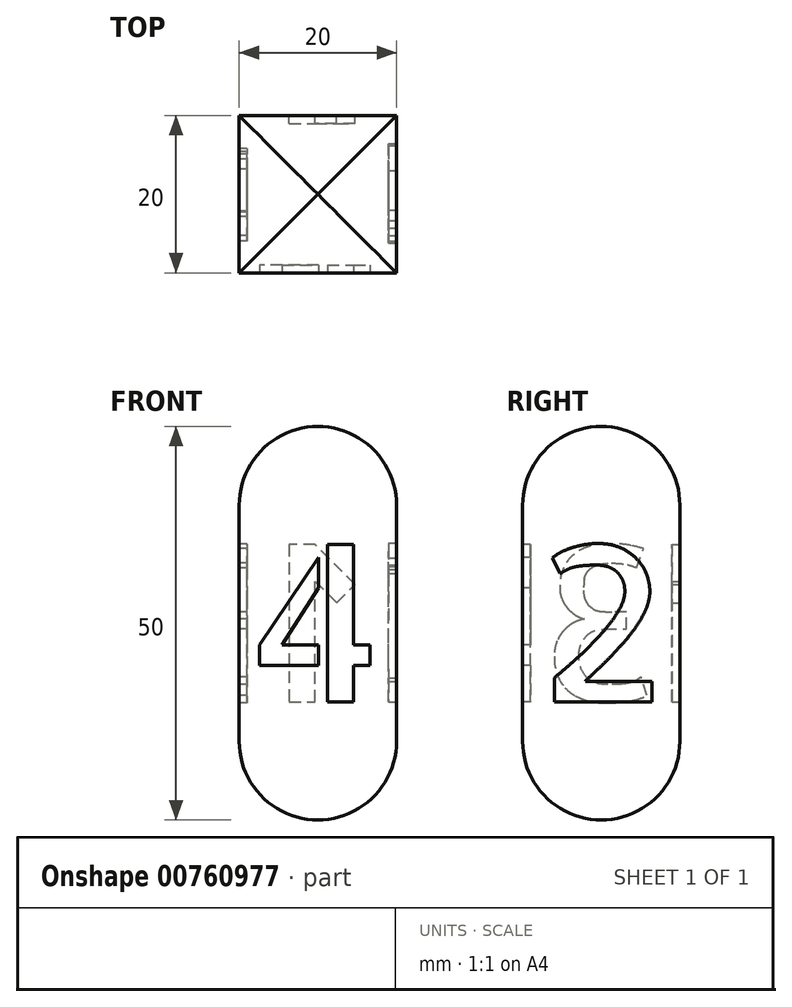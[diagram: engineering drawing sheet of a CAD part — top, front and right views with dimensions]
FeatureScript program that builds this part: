
annotation { "Feature Type Name" : "Feature", "Feature Type Description" : "" }
export const myFeature = defineFeature(function(context is Context, id is Id, definition is map)
    precondition{}
    {
        {
            var Q0;
            Q0=qCreatedBy(makeId("Top.planeOp"),FACE);
            var sketch = newSketch(context, id + "F0", { "sketchPlane" : qUnion([Q0])});
            skLineSegment(sketch, "E0.bottom", {"start": v(0, 0) * mm, "end": v(-20, 0) * mm});
            skLineSegment(sketch, "E0.top", {"start": v(0, 20) * mm, "end": v(-20, 20) * mm});
            skLineSegment(sketch, "E0.left", {"start": v(0, 0) * mm, "end": v(0, 20) * mm});
            skLineSegment(sketch, "E0.right", {"start": v(-20, 0) * mm, "end": v(-20, 20) * mm});
            skSolve(sketch);
        }
        {
            var Q0;
            Q0=makeQuery(id+"F0.imprint","IMPRINT",FACE,{"disambiguationData":[TD([[makeQuery(id+"F0.imprint","IMPRINT",EDGE,{"derivedFrom":sQuery(id+"F0.wireOp",EDGE,"E0.bottom")}),-1.0]])]});
            extrude(context, id + "F1", {"entities" : qUnion([Q0]), "depth" : 50 * mm});
        }
        {
            var Q0;
            Q0=makeQuery(id+"F1.opExtrude","CAP_EDGE",EDGE,{"disambiguationData":[OSD([sQuery(id+"F0.wireOp",EDGE,"E0.top")])],"isStart":false});
            var Q1;
            Q1=makeQuery(id+"F1.opExtrude","CAP_EDGE",EDGE,{"disambiguationData":[OSD([sQuery(id+"F0.wireOp",EDGE,"E0.bottom")])],"isStart":false});
            var Q2;
            Q2=makeQuery(id+"F1.opExtrude","CAP_EDGE",EDGE,{"disambiguationData":[OSD([sQuery(id+"F0.wireOp",EDGE,"E0.right")])],"isStart":false});
            var Q3;
            Q3=makeQuery(id+"F1.opExtrude","CAP_EDGE",EDGE,{"disambiguationData":[OSD([sQuery(id+"F0.wireOp",EDGE,"E0.left")])],"isStart":false});
            fillet(context, id + "F2", {"entities" : qUnion([Q0, Q1, Q2, Q3]), "radius" : 10 * mm, "tangentPropagation" : true, "allowEdgeOverflow" : false});
        }
        {
            var Q0;
            Q0=makeQuery(id+"F1.opExtrude","CAP_EDGE",EDGE,{"disambiguationData":[OSD([sQuery(id+"F0.wireOp",EDGE,"E0.bottom")])],"isStart":true});
            var Q1;
            Q1=makeQuery(id+"F1.opExtrude","CAP_EDGE",EDGE,{"disambiguationData":[OSD([sQuery(id+"F0.wireOp",EDGE,"E0.top")])],"isStart":true});
            var Q2;
            Q2=makeQuery(id+"F1.opExtrude","CAP_EDGE",EDGE,{"disambiguationData":[OSD([sQuery(id+"F0.wireOp",EDGE,"E0.left")])],"isStart":true});
            var Q3;
            Q3=makeQuery(id+"F1.opExtrude","CAP_EDGE",EDGE,{"disambiguationData":[OSD([sQuery(id+"F0.wireOp",EDGE,"E0.right")])],"isStart":true});
            fillet(context, id + "F3", {"entities" : qUnion([Q0, Q1, Q2, Q3]), "radius" : 10 * mm, "tangentPropagation" : true, "allowEdgeOverflow" : false});
        }
        {
            var Q0;
            Q0=makeQuery(id+"F1.opExtrude","SWEPT_FACE",FACE,{"disambiguationData":[OSD([sQuery(id+"F0.wireOp",EDGE,"E0.top")])]});
            var sketch = newSketch(context, id + "F4", { "sketchPlane" : qUnion([Q0])});
            skText(sketch, "E1", { "text": "1", "fontName": "AllertaStencil-Regular.ttf"});
            skLineSegment(sketch, "E2", {"start": v(0, 15) * mm, "end": v(20, 15) * mm, "construction": true});
            skLineSegment(sketch, "E3", {"start": v(3.95, 10) * mm, "end": v(3.95, 15) * mm, "construction": true});
            skLineSegment(sketch, "E4", {"start": v(0, 35) * mm, "end": v(20, 35) * mm, "construction": true});
            skLineSegment(sketch, "E5", {"start": v(3.05, 35) * mm, "end": v(3.05, 40) * mm, "construction": true});
            skLineSegment(sketch, "E6", {"start": v(15.51, 25) * mm, "end": v(20, 25) * mm, "construction": true});
            skLineSegment(sketch, "E7", {"start": v(4.49, 25.65) * mm, "end": v(0, 25.65) * mm, "construction": true});
            const initialGuessF4  = {"E1": [0.00449, 0.015, 1, 0, 0.02]};
            skSetInitialGuess(sketch, initialGuessF4);
            skSolve(sketch);
        }
        {
            var Q0;
            Q0=makeQuery(id+"F1.opExtrude","SWEPT_FACE",FACE,{"disambiguationData":[OSD([sQuery(id+"F0.wireOp",EDGE,"E0.left")])]});
            var sketch = newSketch(context, id + "F5", { "sketchPlane" : qUnion([Q0])});
            skLineSegment(sketch, "E8", {"start": v(20, 15) * mm, "end": v(0, 15) * mm, "construction": true});
            skLineSegment(sketch, "E9", {"start": v(20, 35) * mm, "end": v(0, 35) * mm, "construction": true});
            skLineSegment(sketch, "E10", {"start": v(10, 10) * mm, "end": v(10, 15) * mm, "construction": true});
            skLineSegment(sketch, "E11", {"start": v(9, 40) * mm, "end": v(9, 35) * mm, "construction": true});
            skText(sketch, "E12", { "text": "2", "fontName": "AllertaStencil-Regular.ttf"});
            skLineSegment(sketch, "E13", {"start": v(18.32, 25.83) * mm, "end": v(20, 25.83) * mm, "construction": true});
            skLineSegment(sketch, "E14", {"start": v(0, 25.73) * mm, "end": v(1.68, 25.73) * mm, "construction": true});
            skPoint(sketch, "E14.endSnap0", {"position": v(1.68, 25) * mm});
            const initialGuessF5  = {"E12": [0.00168, 0.015, 1, 0, 0.02]};
            skSetInitialGuess(sketch, initialGuessF5);
            skSolve(sketch);
        }
        {
            var Q0;
            Q0=makeQuery(id+"F1.opExtrude","SWEPT_FACE",FACE,{"disambiguationData":[OSD([sQuery(id+"F0.wireOp",EDGE,"E0.bottom")])]});
            var sketch = newSketch(context, id + "F6", { "sketchPlane" : qUnion([Q0])});
            skLineSegment(sketch, "E15", {"start": v(-20, 35) * mm, "end": v(0, 35) * mm, "construction": true});
            skLineSegment(sketch, "E16", {"start": v(-20, 15) * mm, "end": v(0, 15) * mm, "construction": true});
            skLineSegment(sketch, "E17", {"start": v(-10, 35) * mm, "end": v(-10, 40) * mm, "construction": true});
            skLineSegment(sketch, "E18", {"start": v(-10, 10) * mm, "end": v(-10, 15) * mm, "construction": true});
            skText(sketch, "E19", { "text": "4", "fontName": "AllertaStencil-Regular.ttf"});
            skLineSegment(sketch, "E20", {"start": v(-1.53, 25) * mm, "end": v(0, 25) * mm, "construction": true});
            skLineSegment(sketch, "E21", {"start": v(-18.47, 25.61) * mm, "end": v(-20, 25.61) * mm, "construction": true});
            const initialGuessF6  = {"E19": [-0.01847, 0.015, 1, 0, 0.02]};
            skSetInitialGuess(sketch, initialGuessF6);
            skSolve(sketch);
        }
        {
            var Q0;
            Q0=makeQuery(id+"F1.opExtrude","SWEPT_FACE",FACE,{"disambiguationData":[OSD([sQuery(id+"F0.wireOp",EDGE,"E0.right")])]});
            var sketch = newSketch(context, id + "F7", { "sketchPlane" : qUnion([Q0])});
            skLineSegment(sketch, "E22", {"start": v(-20, 15) * mm, "end": v(0, 15) * mm, "construction": true});
            skLineSegment(sketch, "E23", {"start": v(0, 35) * mm, "end": v(-20, 35) * mm, "construction": true});
            skLineSegment(sketch, "E24", {"start": v(-11.24, 40) * mm, "end": v(-11.24, 35) * mm, "construction": true});
            skLineSegment(sketch, "E25", {"start": v(-12.04, 10) * mm, "end": v(-12.04, 15) * mm, "construction": true});
            skText(sketch, "E26", { "text": "3", "fontName": "AllertaStencil-Regular.ttf"});
            skLineSegment(sketch, "E27", {"start": v(-2.17, 25) * mm, "end": v(0, 25) * mm, "construction": true});
            skLineSegment(sketch, "E28", {"start": v(-17.83, 25.74) * mm, "end": v(-20, 25.74) * mm, "construction": true});
            const initialGuessF7  = {"E26": [-0.01783, 0.015, 1, 0, 0.02]};
            skSetInitialGuess(sketch, initialGuessF7);
            skSolve(sketch);
        }
        {
            var Q0;
            Q0=qSketchRegion(id+"F4",true);
            extrude(context, id + "F8", {"entities" : qUnion([Q0]), "operationType" : NewBodyOperationType.REMOVE, "oppositeDirection" : true, "depth" : 1 * mm});
        }
        {
            var Q0;
            Q0=qSketchRegion(id+"F5",true);
            extrude(context, id + "F9", {"entities" : qUnion([Q0]), "operationType" : NewBodyOperationType.REMOVE, "oppositeDirection" : true, "depth" : 1 * mm});
        }
        {
            var Q0;
            Q0=qSketchRegion(id+"F6",true);
            extrude(context, id + "F10", {"entities" : qUnion([Q0]), "operationType" : NewBodyOperationType.REMOVE, "oppositeDirection" : true, "depth" : 1 * mm});
        }
        {
            var Q0;
            Q0=qSketchRegion(id+"F7",true);
            extrude(context, id + "F11", {"entities" : qUnion([Q0]), "operationType" : NewBodyOperationType.REMOVE, "oppositeDirection" : true, "depth" : 1 * mm});
        }
    });
